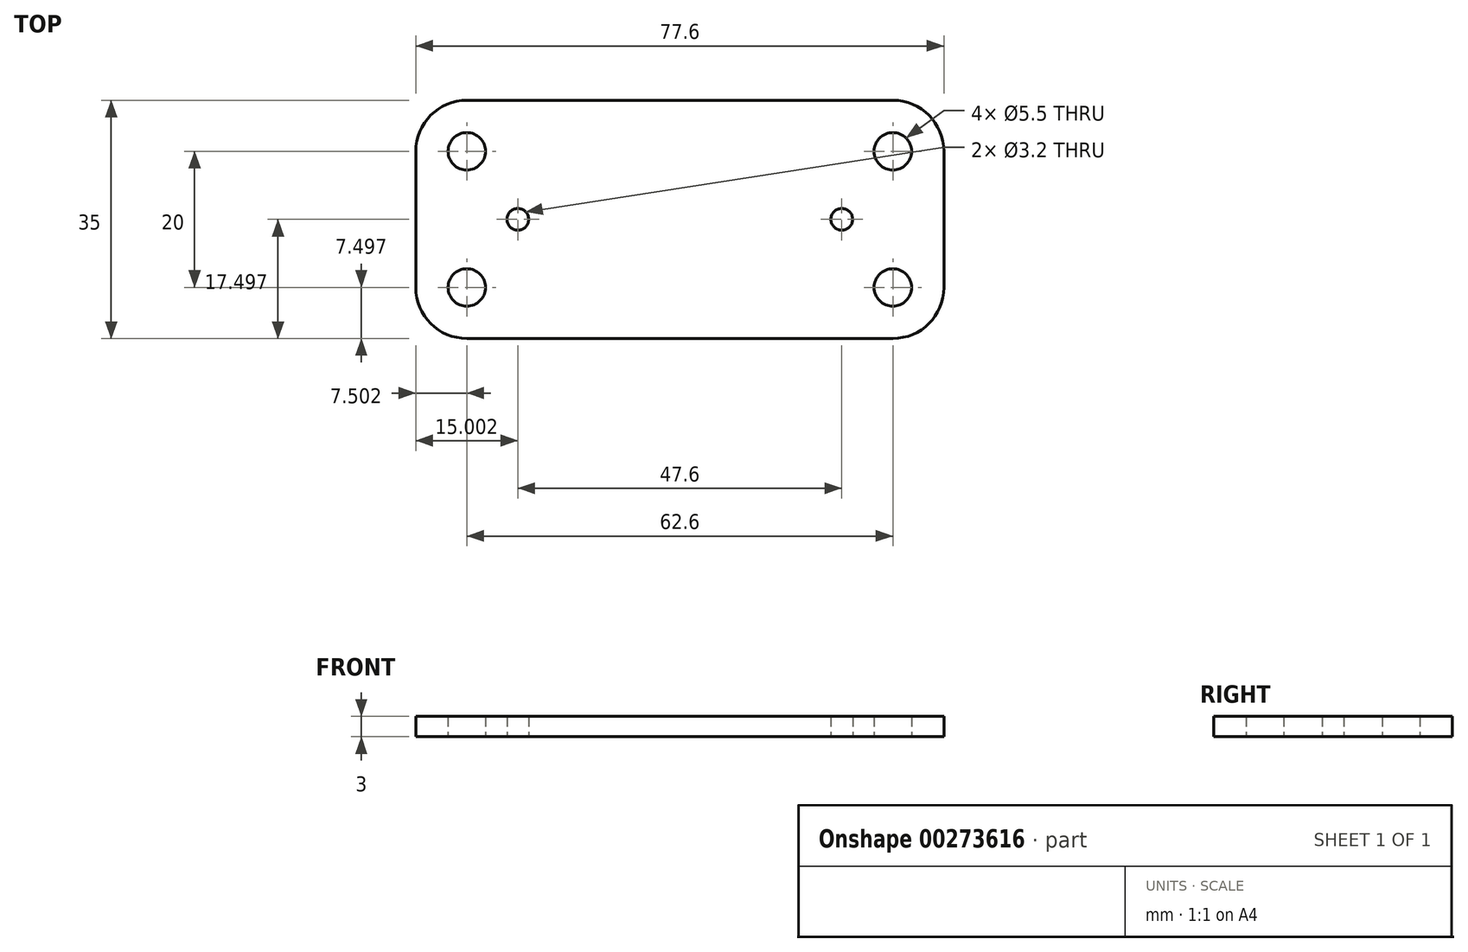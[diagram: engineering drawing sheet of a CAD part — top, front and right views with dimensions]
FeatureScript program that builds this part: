
annotation { "Feature Type Name" : "Feature", "Feature Type Description" : "" }
export const myFeature = defineFeature(function(context is Context, id is Id, definition is map)
    precondition{}
    {
        {
            var Q0;
            Q0=qCreatedBy(makeId("Top.planeOp"),FACE);
            var sketch = newSketch(context, id + "F0", { "sketchPlane" : qUnion([Q0])});
            skLineSegment(sketch, "E0.bottom", {"start": v(-28.46, 16.8) * mm, "end": v(49.14, 16.8) * mm});
            skLineSegment(sketch, "E0.top", {"start": v(-28.46, -18.2) * mm, "end": v(49.14, -18.2) * mm});
            skLineSegment(sketch, "E0.left", {"start": v(-28.46, 16.8) * mm, "end": v(-28.46, -18.2) * mm});
            skLineSegment(sketch, "E0.right", {"start": v(49.14, 16.8) * mm, "end": v(49.14, -18.2) * mm});
            skPoint(sketch, "E1", {"position": v(-13.46, -0.7) * mm});
            skPoint(sketch, "E2", {"position": v(34.14, -0.7) * mm});
            skPoint(sketch, "E3", {"position": v(-20.96, 9.3) * mm});
            skPoint(sketch, "E4", {"position": v(-20.96, -10.7) * mm});
            skPoint(sketch, "E5", {"position": v(41.64, 9.3) * mm});
            skPoint(sketch, "E6", {"position": v(41.64, -10.7) * mm});
            skPoint(sketch, "E7", {"position": v(49.14, -0.7) * mm});
            skCircle(sketch, "E8", {"center": v(-20.96, 9.3) * mm, "radius": 7.5 * mm});
            skCircle(sketch, "E9", {"center": v(-20.96, -10.7) * mm, "radius": 7.5 * mm});
            skCircle(sketch, "E10", {"center": v(41.64, -10.7) * mm, "radius": 7.5 * mm});
            skCircle(sketch, "E11", {"center": v(41.64, 9.3) * mm, "radius": 7.5 * mm});
            skSolve(sketch);
        }
        {
            var Q0;
            {var subQ5=sQuery(id+"F0.wireOp",EDGE,"E8");var subQ13=sQuery(id+"F0.wireOp",EDGE,"E0.bottom");var subQ14=makeQuery(id+"F0.imprint","INTERSECT",VERTEX,{"derivedFrom":[subQ13,subQ5]});Q0=makeQuery(id+"F0.imprint","IMPRINT",FACE,{"disambiguationData":[TD([[makeQuery(id+"F0.imprint","IMPRINT",EDGE,{"disambiguationData":[TD([[subQ14,-1.0]])],"derivedFrom":subQ13}),-1.0]])]});}
            var Q1;
            {var subQ0=sQuery(id+"F0.wireOp",EDGE,"E11");var subQ1=makeQuery(id+"F0.imprint","INTERSECT",VERTEX,{"derivedFrom":[sQuery(id+"F0.wireOp",EDGE,"E0.bottom"),subQ0]});Q1=makeQuery(id+"F0.imprint","IMPRINT",FACE,{"disambiguationData":[TD([[makeQuery(id+"F0.imprint","IMPRINT",EDGE,{"disambiguationData":[TD([[subQ1,1.0]])],"derivedFrom":subQ0}),1.0]])]});}
            var Q2;
            {var subQ0=sQuery(id+"F0.wireOp",EDGE,"E8");var subQ1=makeQuery(id+"F0.imprint","INTERSECT",VERTEX,{"derivedFrom":[sQuery(id+"F0.wireOp",EDGE,"E0.bottom"),subQ0]});Q2=makeQuery(id+"F0.imprint","IMPRINT",FACE,{"disambiguationData":[TD([[makeQuery(id+"F0.imprint","IMPRINT",EDGE,{"disambiguationData":[TD([[subQ1,-1.0]])],"derivedFrom":subQ0}),1.0]])]});}
            var Q3;
            {var subQ0=sQuery(id+"F0.wireOp",EDGE,"E9");var subQ1=makeQuery(id+"F0.imprint","INTERSECT",VERTEX,{"derivedFrom":[sQuery(id+"F0.wireOp",EDGE,"E0.top"),subQ0]});Q3=makeQuery(id+"F0.imprint","IMPRINT",FACE,{"disambiguationData":[TD([[makeQuery(id+"F0.imprint","IMPRINT",EDGE,{"disambiguationData":[TD([[subQ1,1.0]])],"derivedFrom":subQ0}),1.0]])]});}
            var Q4;
            {var subQ0=sQuery(id+"F0.wireOp",EDGE,"E10");var subQ1=makeQuery(id+"F0.imprint","INTERSECT",VERTEX,{"derivedFrom":[sQuery(id+"F0.wireOp",EDGE,"E0.top"),subQ0]});Q4=makeQuery(id+"F0.imprint","IMPRINT",FACE,{"disambiguationData":[TD([[makeQuery(id+"F0.imprint","IMPRINT",EDGE,{"disambiguationData":[TD([[subQ1,1.0]])],"derivedFrom":subQ0}),1.0]])]});}
            extrude(context, id + "F1", {"entities" : qUnion([Q0, Q1, Q2, Q3, Q4]), "depth" : 3 * mm});
        }
        {
            var Q0;
            Q0=sQuery(id+"F0.wireOp",VERTEX,"E3");
            var Q1;
            Q1=sQuery(id+"F0.wireOp",VERTEX,"E4");
            var Q2;
            Q2=sQuery(id+"F0.wireOp",VERTEX,"E6");
            var Q3;
            Q3=sQuery(id+"F0.wireOp",VERTEX,"E5");
            var Q4;
            Q4=makeQuery(id+"F1.opExtrude","SWEPT_BODY",BODY,{"disambiguationData":[OSD([sQuery(id+"F0.wireOp",EDGE,"E0.bottom"),sQuery(id+"F0.wireOp",EDGE,"E0.top"),sQuery(id+"F0.wireOp",EDGE,"E0.left"),sQuery(id+"F0.wireOp",EDGE,"E0.right")])]});
            hole(context, id + "F2", {"style" : HoleStyle.SIMPLE, "endStyle" : HoleEndStyle.THROUGH, "oppositeDirection" : true, "standardTappedOrClearance" : lookupTablePath({ "standard" : "ISO", "fit" : "Normal", "size" : "M5", "type" : "Clearance" }), "standardBlindInLast" : lookupTablePath({ "fit" : "Standard", "standard" : "ISO", "size" : "M5", "type" : "Clearance" }), "holeDiameter" : 5.5 * mm, "tappedDepth" : 13.2 * mm, "tapClearance" : 3, "startFromSketch" : true, "locations" : qUnion([Q0, Q1, Q2, Q3]), "scope" : qUnion([Q4])});
        }
        {
            var Q0;
            Q0=sQuery(id+"F0.wireOp",VERTEX,"E1");
            var Q1;
            Q1=sQuery(id+"F0.wireOp",VERTEX,"E2");
            var Q2;
            Q2=makeQuery(id+"F1.opExtrude","SWEPT_BODY",BODY,{"disambiguationData":[OSD([sQuery(id+"F0.wireOp",EDGE,"E0.bottom"),sQuery(id+"F0.wireOp",EDGE,"E0.top"),sQuery(id+"F0.wireOp",EDGE,"E0.left"),sQuery(id+"F0.wireOp",EDGE,"E0.right")])]});
            hole(context, id + "F3", {"style" : HoleStyle.SIMPLE, "endStyle" : HoleEndStyle.THROUGH, "oppositeDirection" : true, "standardTappedOrClearance" : lookupTablePath({ "standard" : "ISO", "engagement" : "75%", "pitch" : "0.75 mm", "size" : "M4", "type" : "Tapped" }), "standardBlindInLast" : lookupTablePath({ "standard" : "ISO", "engagement" : "75%", "pitch" : "0.75 mm", "size" : "M4", "type" : "Tapped" }), "holeDiameter" : 3.2 * mm, "showTappedDepth" : true, "tappedDepth" : 13.2 * mm, "tapClearance" : 3, "startFromSketch" : true, "locations" : qUnion([Q0, Q1]), "scope" : qUnion([Q2])});
        }
    });
